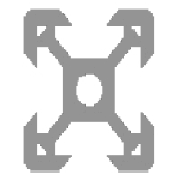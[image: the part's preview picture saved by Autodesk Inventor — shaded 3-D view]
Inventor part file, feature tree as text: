
AUTODESK INVENTOR PART (.ipt)
format: ipt  version: 2013 (Build 170138000, 138)  size: 187,904 bytes
history: native  units: mm
features: other x4, sketch x2, plane x1
ambient origin geometry x8: Origin, YZ Plane, XZ Plane, XY Plane, X Axis, Y Axis, Z Axis, Center Point
bodies: Solid1 (feature_tree), Body (feature_tree)
feature tree (7):
  other  "Driven Length"
  other  "Frame Generator"
  other  "Start Plane"
  other  "End Plane"
  sketch  "Sketch4"  dims[d2=4.2mm]
  plane  "Work Plane4"
  sketch  "Sketch5"  dims[d3=1.5mm d4=1.64mm d5=1.8mm d6=5.68mm d7=1.8mm d9=1.5mm d12=-0.0mm d13=275.0mm d14=0.13mm d15=0.0mm d18=90.0deg d17=275.0mm]
